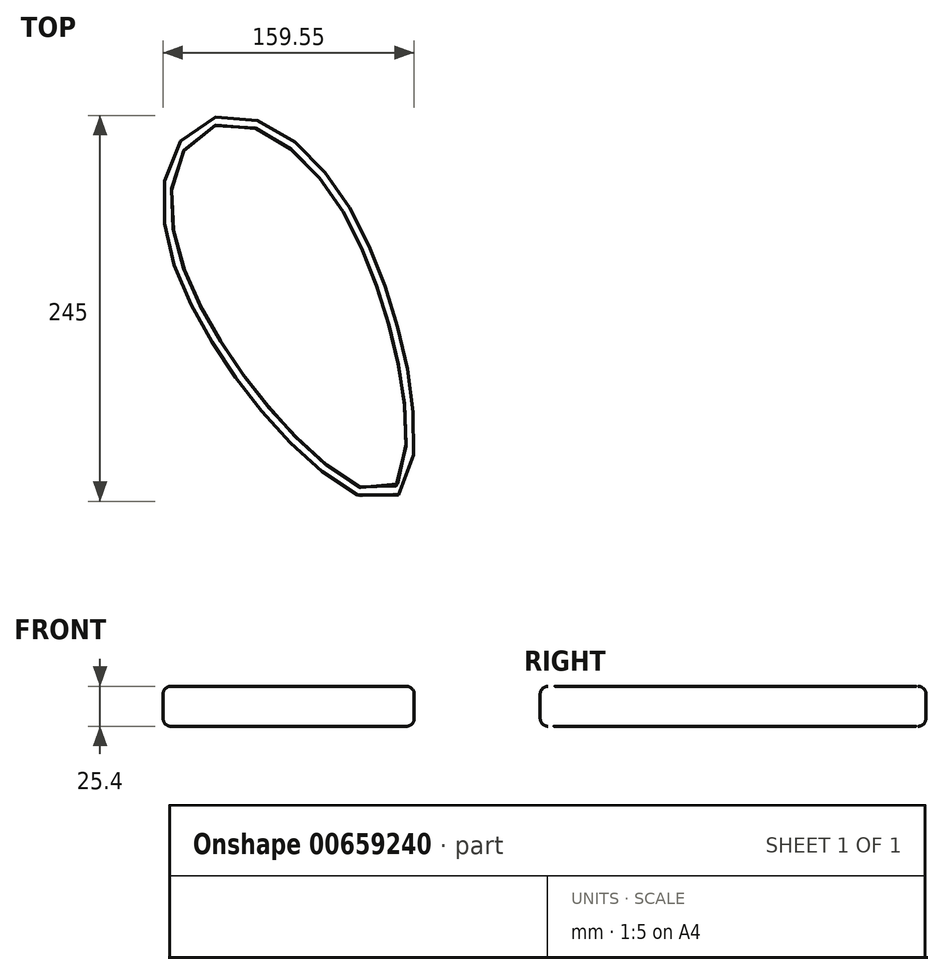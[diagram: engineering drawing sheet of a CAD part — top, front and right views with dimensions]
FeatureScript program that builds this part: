
annotation { "Feature Type Name" : "Feature", "Feature Type Description" : "" }
export const myFeature = defineFeature(function(context is Context, id is Id, definition is map)
    precondition{}
    {
        {
            var Q0;
            Q0=qCreatedBy(makeId("Top.planeOp"),FACE);
            var sketch = newSketch(context, id + "F0", { "sketchPlane" : qUnion([Q0])});
            skFitSpline(sketch, "E0", {"points": [v(0, 0) * mm, v(-89.82, 55.93) * mm, v(-112.24, -33.9) * mm, v(26.65, -185.39) * mm, v(0, 0) * mm]});
            skSolve(sketch);
        }
        {
            var Q0;
            Q0=makeQuery(id+"F0.imprint","IMPRINT",FACE,{"disambiguationData":[TD([[makeQuery(id+"F0.imprint","IMPRINT",EDGE,{"derivedFrom":sQuery(id+"F0.wireOp",EDGE,"E0")}),1.0]])]});
            extrude(context, id + "F1", {"entities" : qUnion([Q0]), "depth" : 25.4 * mm, "offsetDistance" : 25.4 * mm});
        }
        {
            var Q0;
            Q0=makeQuery(id+"F1.opExtrude","CAP_FACE",FACE,{"disambiguationData":[OSD([sQuery(id+"F0.wireOp",EDGE,"E0")])],"isStart":false});
            fillet(context, id + "F2", {"entities" : qUnion([Q0]), "radius" : 5 * mm, "tangentPropagation" : true, "allowEdgeOverflow" : false});
        }
        {
            var Q0;
            Q0=makeQuery(id+"F1.opExtrude","CAP_FACE",FACE,{"disambiguationData":[OSD([sQuery(id+"F0.wireOp",EDGE,"E0")])],"isStart":true});
            fillet(context, id + "F3", {"entities" : qUnion([Q0]), "radius" : 5 * mm, "tangentPropagation" : true, "allowEdgeOverflow" : false});
        }
    });
